# Revit family: ShowerHead-18Lmin-Vitra-LiteLSSeries-A45674
name_source: partatom
category: Plumbing Fixtures
revit_build: Autodesk Revit 2017 (Build: 20160225_1515(x64)
units: mm (PartAtom-declared; Revit-internal decimal feet)

## family parameters
Always vertical = No
Cut with Voids When Loaded = No
OmniClass Number = 23.45.00.00
OmniClass Title = Sanitary, Laundry, and Cleaning Equipment
Part Type = Normal
Room Calculation Point = No
Round Connector Dimension = Use Diameter
Shared = Yes
Work Plane-Based = Yes

## types (2) — shared parameters
BIMobject category = Bath/Shower Mixer
Brand = Artema
CW Connection = No
Connection Diameter (mm) = 20 mm  [stored 0.0656168 ft]
Description = Shower Head
Design country = Turkey
HW Connection = No
IFC Classification = Sanitary Terminal
Main Material = Metal
Manufacturer = Vitra
Manufacturer name = Vitra
Masterformat 2014 Code = 22 41 23
Masterformat 2014 Description = Residential Showers
Mounting type = Pipe Connect
NBS Referans Code = 35-06-81
NBS Referans Description = Shower Heads
Nominal Depth (mm) = 300 mm
Nominal Height (mm) = 54 mm  [stored 0.177165 ft]
Nominal Width (mm) = 300 mm
Number Of Connections = 1
OmniClass Code = 23-31 17 19
OmniClass Description = Shower Head Fixtures
Product Type = Showerhead
Product certification = https://www.vitraglobal.com
Product family = Lite LS Series
Product group = Showers Head
Product url = https://www.vitra.com.tr
Secondary Material = Plastic
Technical description = https://www.vitra.com.tr
URL = https://vitraglobal.com
Uniclass 1.4 Code = L7214
Uniclass 1.4 Description = Showers
Uniclass 2.0 Code = PR-35-06-81
Uniclass 2.0 Description = Shower Heads
Uniclass 2015 Code = Pr_40_20_87_76
Uniclass 2015 Name = Shower heads
Uniformat II Code = D2010
Uniformat II Description = Plumbing Fixtures
Vent Connection = No
Warranty Period (Year) = 5 Years
Waste Connection = No
Weight Net (kg) = 0.4
Youtube = https://www.youtube.com
zero-valued in all types: Default Elevation

## per-type parameters (varying)
| type | Article No. (default) | Coating Material | Color | Model | Product SKU |
| ShowerHead-18Lmin-Vitra-LiteLSSeries-A45674 | A45674 | Chrome | Chrome | A45674 | A45674 |
| ShowerHead-18Lmin-Vitra-LiteLSSeries-A4567423 | A4567423 | Gold | Gold | A4567423 | A4567423 |

note: [stored X ft] marks values corroborated as IEEE doubles in the binary element streams (Revit-internal decimal feet)

## geometry (parser evidence)
native form markers: Sweep x3
no freeform markers — native parametric forms only
